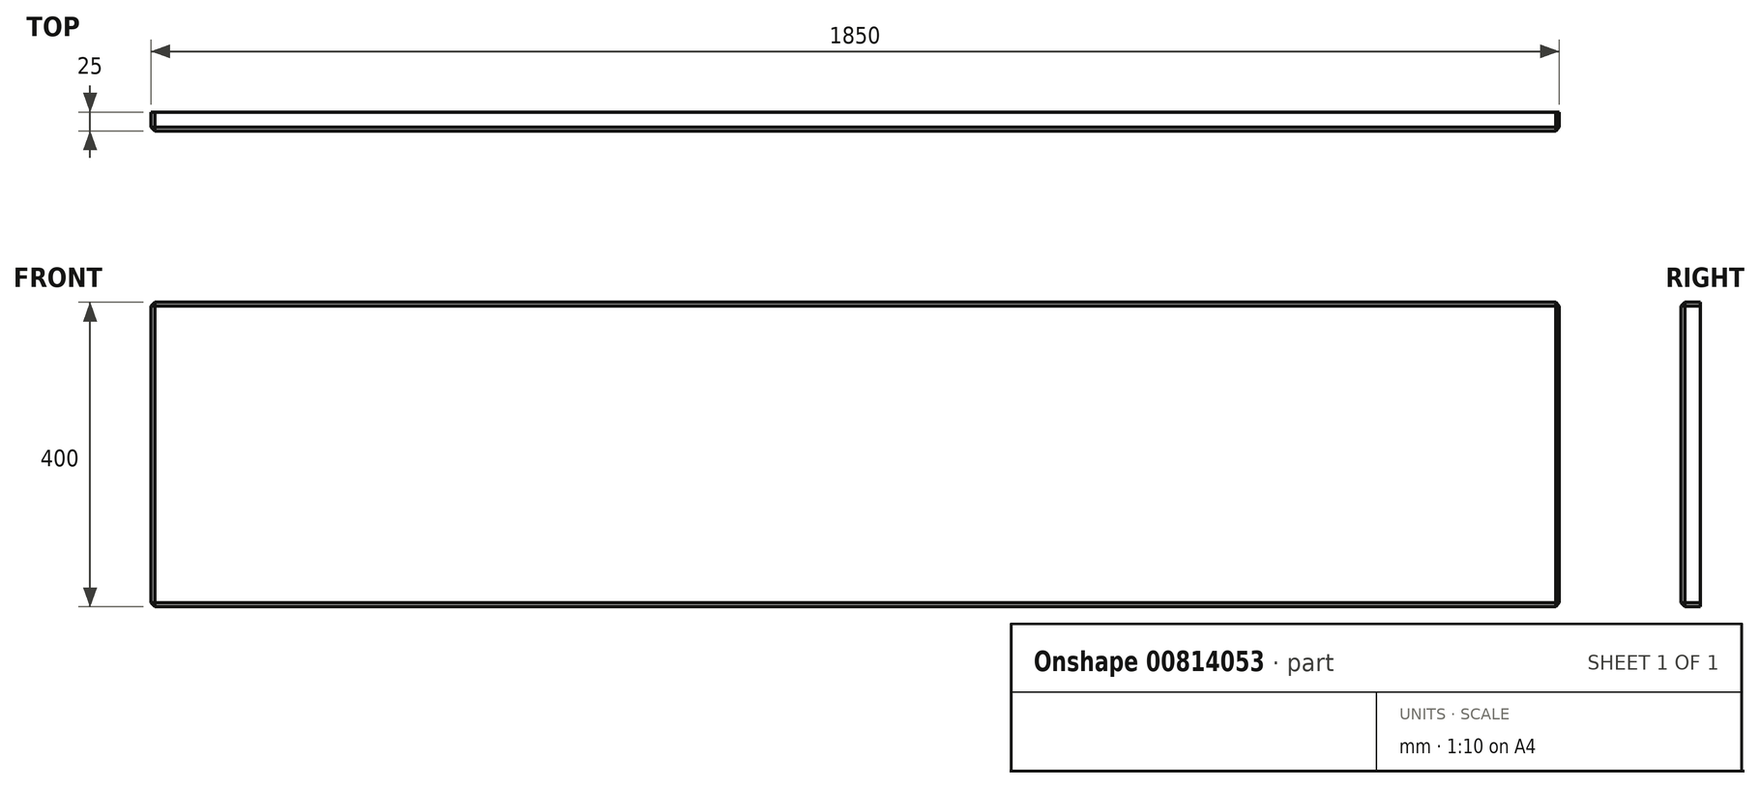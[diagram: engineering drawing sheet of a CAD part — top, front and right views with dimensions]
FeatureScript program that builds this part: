
annotation { "Feature Type Name" : "Feature", "Feature Type Description" : "" }
export const myFeature = defineFeature(function(context is Context, id is Id, definition is map)
    precondition{}
    {
        {
            var Q0;
            Q0=qCreatedBy(makeId("Front.planeOp"),FACE);
            var sketch = newSketch(context, id + "F0", { "sketchPlane" : qUnion([Q0])});
            skLineSegment(sketch, "E0.bottom", {"start": v(-925, 200) * mm, "end": v(925, 200) * mm});
            skLineSegment(sketch, "E0.top", {"start": v(-925, -200) * mm, "end": v(925, -200) * mm});
            skLineSegment(sketch, "E0.left", {"start": v(-925, 200) * mm, "end": v(-925, -200) * mm});
            skLineSegment(sketch, "E0.right", {"start": v(925, 200) * mm, "end": v(925, -200) * mm});
            skPoint(sketch, "E0.middle", {"position": v(0, 0) * mm});
            skSolve(sketch);
        }
        {
            var Q0;
            Q0 = qSketchRegion(id + "F0", true);
            extrude(context, id + "F1", {"entities" : qUnion([Q0]), "depth" : 25 * mm, "offsetDistance" : 25 * mm});
        }
        {
            var Q0;
            Q0=makeQuery(id+"F1.opExtrude","CAP_EDGE",EDGE,{"disambiguationData":[OSD([sQuery(id+"F0.wireOp",EDGE,"E0.bottom")])],"isStart":false});
            var Q1;
            Q1=makeQuery(id+"F1.opExtrude","CAP_EDGE",EDGE,{"disambiguationData":[OSD([sQuery(id+"F0.wireOp",EDGE,"E0.left")])],"isStart":false});
            var Q2;
            Q2=makeQuery(id+"F1.opExtrude","CAP_EDGE",EDGE,{"disambiguationData":[OSD([sQuery(id+"F0.wireOp",EDGE,"E0.top")])],"isStart":false});
            var Q3;
            Q3=makeQuery(id+"F1.opExtrude","CAP_EDGE",EDGE,{"disambiguationData":[OSD([sQuery(id+"F0.wireOp",EDGE,"E0.right")])],"isStart":false});
            var Q4;
            Q4=makeQuery(id+"F1.opExtrude","SWEPT_EDGE",EDGE,{"disambiguationData":[OSD([sQuery(id+"F0.wireOp",EDGE,"E0.bottom"),sQuery(id+"F0.wireOp",EDGE,"E0.left")])]});
            var Q5;
            Q5=makeQuery(id+"F1.opExtrude","SWEPT_EDGE",EDGE,{"disambiguationData":[OSD([sQuery(id+"F0.wireOp",EDGE,"E0.top"),sQuery(id+"F0.wireOp",EDGE,"E0.left")])]});
            var Q6;
            Q6=makeQuery(id+"F1.opExtrude","SWEPT_EDGE",EDGE,{"disambiguationData":[OSD([sQuery(id+"F0.wireOp",EDGE,"E0.top"),sQuery(id+"F0.wireOp",EDGE,"E0.right")])]});
            var Q7;
            Q7=makeQuery(id+"F1.opExtrude","SWEPT_EDGE",EDGE,{"disambiguationData":[OSD([sQuery(id+"F0.wireOp",EDGE,"E0.bottom"),sQuery(id+"F0.wireOp",EDGE,"E0.right")])]});
            chamfer(context, id + "F2", {"entities" : qUnion([Q0, Q1, Q2, Q3, Q4, Q5, Q6, Q7]), "width" : 5 * mm, "tangentPropagation" : true});
        }
    });
